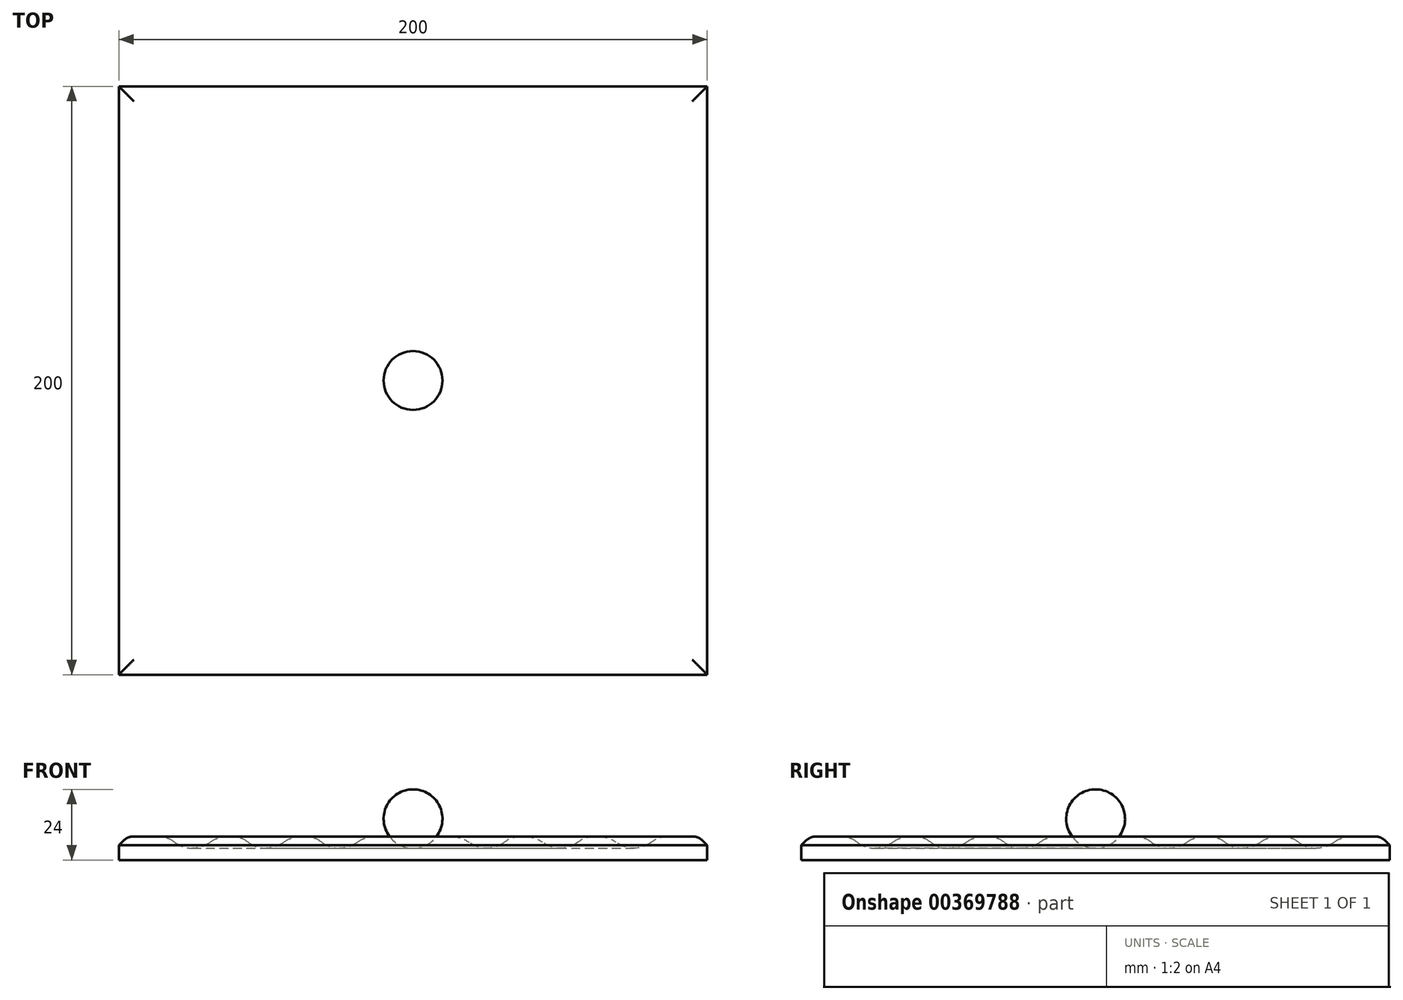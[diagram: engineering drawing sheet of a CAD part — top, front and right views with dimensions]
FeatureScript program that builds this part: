
annotation { "Feature Type Name" : "Feature", "Feature Type Description" : "" }
export const myFeature = defineFeature(function(context is Context, id is Id, definition is map)
    precondition{}
    {
        {
            var Q0;
            Q0=qCreatedBy(makeId("Top.planeOp"),FACE);
            var sketch = newSketch(context, id + "F0", { "sketchPlane" : qUnion([Q0])});
            skLineSegment(sketch, "E0.bottom", {"start": v(100, -100) * mm, "end": v(-100, -100) * mm});
            skLineSegment(sketch, "E0.top", {"start": v(100, 100) * mm, "end": v(-100, 100) * mm});
            skLineSegment(sketch, "E0.left", {"start": v(100, -100) * mm, "end": v(100, 100) * mm});
            skLineSegment(sketch, "E0.right", {"start": v(-100, -100) * mm, "end": v(-100, 100) * mm});
            skPoint(sketch, "E0.middle", {"position": v(0, 0) * mm});
            skCircle(sketch, "E1", {"center": v(0, 0) * mm, "radius": 90 * mm});
            skSolve(sketch);
        }
        {
            var Q0;
            Q0=makeQuery(id+"F0.imprint","IMPRINT",FACE,{"disambiguationData":[TD([[makeQuery(id+"F0.imprint","IMPRINT",EDGE,{"derivedFrom":sQuery(id+"F0.wireOp",EDGE,"E0.bottom")}),-1.0]])]});
            var Q1;
            Q1=makeQuery(id+"F0.imprint","IMPRINT",FACE,{"disambiguationData":[TD([[makeQuery(id+"F0.imprint","IMPRINT",EDGE,{"derivedFrom":sQuery(id+"F0.wireOp",EDGE,"E1")}),1.0]])]});
            extrude(context, id + "F1", {"entities" : qUnion([Q0, Q1]), "depth" : 8 * mm});
        }
        {
            var Q0;
            Q0=qCreatedBy(makeId("Front.planeOp"),FACE);
            var sketch = newSketch(context, id + "F2", { "sketchPlane" : qUnion([Q0])});
            skLineSegment(sketch, "E2", {"start": v(0, 0) * mm, "end": v(0, 24) * mm});
            skArc(sketch, "E3", {"start": v(0, 4) * mm, "mid": v(10, 14) * mm, "end": v(0, 24) * mm});
            skArc(sketch, "E4.1.0.0", {"start": v(25, 4) * mm, "mid": v(35, 14) * mm, "end": v(25, 24) * mm});
            skLineSegment(sketch, "E4.1.0.1", {"start": v(25, 0) * mm, "end": v(25, 24) * mm});
            skArc(sketch, "E4.2.0.0", {"start": v(50, 4) * mm, "mid": v(60, 14) * mm, "end": v(50, 24) * mm});
            skLineSegment(sketch, "E4.2.0.1", {"start": v(50, 0) * mm, "end": v(50, 24) * mm});
            skArc(sketch, "E4.3.0.0", {"start": v(75, 4) * mm, "mid": v(85, 14) * mm, "end": v(75, 24) * mm});
            skLineSegment(sketch, "E4.3.0.1", {"start": v(75, 0) * mm, "end": v(75, 24) * mm});
            skLineSegment(sketch, "E4.direction1", {"start": v(0, 4) * mm, "end": v(25, 4) * mm, "construction": true});
            skArc(sketch, "E5.1.0.0", {"start": v(-25, 4) * mm, "mid": v(-15, 14) * mm, "end": v(-25, 24) * mm});
            skLineSegment(sketch, "E5.1.0.1", {"start": v(-25, 0) * mm, "end": v(-25, 24) * mm});
            skArc(sketch, "E5.2.0.0", {"start": v(-50, 4) * mm, "mid": v(-40, 14) * mm, "end": v(-50, 24) * mm});
            skLineSegment(sketch, "E5.2.0.1", {"start": v(-50, 0) * mm, "end": v(-50, 24) * mm});
            skArc(sketch, "E5.3.0.0", {"start": v(-75, 4) * mm, "mid": v(-65, 14) * mm, "end": v(-75, 24) * mm});
            skLineSegment(sketch, "E5.3.0.1", {"start": v(-75, 0) * mm, "end": v(-75, 24) * mm});
            skLineSegment(sketch, "E5.direction1", {"start": v(0, 4) * mm, "end": v(-25, 4) * mm, "construction": true});
            skSolve(sketch);
        }
        {
            var Q0;
            {var subQ0=sQuery(id+"F2.wireOp",EDGE,"E3");Q0=makeQuery(id+"F2.imprint","IMPRINT",FACE,{"disambiguationData":[TD([[makeQuery(id+"F2.imprint","IMPRINT",EDGE,{"derivedFrom":subQ0}),1.0]])]});}
            var Q1;
            {var subQ0=sQuery(id+"F2.wireOp",EDGE,"E5.1.0.0");Q1=makeQuery(id+"F2.imprint","IMPRINT",FACE,{"disambiguationData":[TD([[makeQuery(id+"F2.imprint","IMPRINT",EDGE,{"derivedFrom":subQ0}),1.0]])]});}
            var Q2;
            {var subQ0=sQuery(id+"F2.wireOp",EDGE,"E5.2.0.0");Q2=makeQuery(id+"F2.imprint","IMPRINT",FACE,{"disambiguationData":[TD([[makeQuery(id+"F2.imprint","IMPRINT",EDGE,{"derivedFrom":subQ0}),1.0]])]});}
            var Q3;
            {var subQ0=sQuery(id+"F2.wireOp",EDGE,"E5.3.0.0");Q3=makeQuery(id+"F2.imprint","IMPRINT",FACE,{"disambiguationData":[TD([[makeQuery(id+"F2.imprint","IMPRINT",EDGE,{"derivedFrom":subQ0}),1.0]])]});}
            var Q4;
            {var subQ0=sQuery(id+"F2.wireOp",EDGE,"E4.1.0.0");Q4=makeQuery(id+"F2.imprint","IMPRINT",FACE,{"disambiguationData":[TD([[makeQuery(id+"F2.imprint","IMPRINT",EDGE,{"derivedFrom":subQ0}),1.0]])]});}
            var Q5;
            {var subQ0=sQuery(id+"F2.wireOp",EDGE,"E4.2.0.0");Q5=makeQuery(id+"F2.imprint","IMPRINT",FACE,{"disambiguationData":[TD([[makeQuery(id+"F2.imprint","IMPRINT",EDGE,{"derivedFrom":subQ0}),1.0]])]});}
            var Q6;
            {var subQ0=sQuery(id+"F2.wireOp",EDGE,"E4.3.0.0");Q6=makeQuery(id+"F2.imprint","IMPRINT",FACE,{"disambiguationData":[TD([[makeQuery(id+"F2.imprint","IMPRINT",EDGE,{"derivedFrom":subQ0}),1.0]])]});}
            var Q7;
            Q7=sQuery(id+"F2.wireOp",EDGE,"E2");
            revolve(context, id + "F3", {"entities" : qUnion([Q0, Q1, Q2, Q3, Q4, Q5, Q6]), "axis" : qUnion([Q7]), "revolveType" : RevolveType.FULL});
        }
        {
            var Q0;
            Q0=makeQuery(id+"F3.opRevolve","SWEPT_BODY",BODY,{"disambiguationData":[OSD([sQuery(id+"F2.wireOp",EDGE,"E4.1.0.0"),sQuery(id+"F2.wireOp",EDGE,"E4.1.0.1")])]});
            var Q1;
            Q1=makeQuery(id+"F3.opRevolve","SWEPT_BODY",BODY,{"disambiguationData":[OSD([sQuery(id+"F2.wireOp",EDGE,"E5.1.0.0"),sQuery(id+"F2.wireOp",EDGE,"E5.1.0.1")])]});
            var Q2;
            Q2=makeQuery(id+"F3.opRevolve","SWEPT_BODY",BODY,{"disambiguationData":[OSD([sQuery(id+"F2.wireOp",EDGE,"E5.2.0.0"),sQuery(id+"F2.wireOp",EDGE,"E5.2.0.1")])]});
            var Q3;
            Q3=makeQuery(id+"F3.opRevolve","SWEPT_BODY",BODY,{"disambiguationData":[OSD([sQuery(id+"F2.wireOp",EDGE,"E4.2.0.0"),sQuery(id+"F2.wireOp",EDGE,"E4.2.0.1")])]});
            var Q4;
            Q4=makeQuery(id+"F3.opRevolve","SWEPT_BODY",BODY,{"disambiguationData":[OSD([sQuery(id+"F2.wireOp",EDGE,"E5.3.0.0"),sQuery(id+"F2.wireOp",EDGE,"E5.3.0.1")])]});
            var Q5;
            Q5=makeQuery(id+"F3.opRevolve","SWEPT_BODY",BODY,{"disambiguationData":[OSD([sQuery(id+"F2.wireOp",EDGE,"E4.3.0.0"),sQuery(id+"F2.wireOp",EDGE,"E4.3.0.1")])]});
            var Q6;
            Q6=makeQuery(id+"F1.opExtrude","SWEPT_BODY",BODY,{"disambiguationData":[OSD([sQuery(id+"F0.wireOp",EDGE,"E0.bottom"),sQuery(id+"F0.wireOp",EDGE,"E0.top"),sQuery(id+"F0.wireOp",EDGE,"E0.left"),sQuery(id+"F0.wireOp",EDGE,"E0.right")])]});
            booleanBodies(context, id + "F4", {"operationType" : BooleanOperationType.SUBTRACTION, "tools" : qUnion([Q0, Q1, Q2, Q3, Q4, Q5]), "targets" : qUnion([Q6])});
        }
        {
            var Q0;
            Q0=makeQuery(id+"F4.opBoolean","INTERSECT",EDGE,{"disambiguationData":[OD(0.0)],"derivedFrom":[makeQuery(id+"F1.opExtrude","CAP_FACE",FACE,{"disambiguationData":[OSD([sQuery(id+"F0.wireOp",EDGE,"E0.bottom"),sQuery(id+"F0.wireOp",EDGE,"E0.top"),sQuery(id+"F0.wireOp",EDGE,"E0.left"),sQuery(id+"F0.wireOp",EDGE,"E0.right")])],"isStart":false}),makeQuery(id+"F3.opRevolve","SWEPT_FACE",FACE,{"disambiguationData":[OSD([sQuery(id+"F2.wireOp",EDGE,"E4.3.0.0")])]})]});
            var Q1;
            Q1=makeQuery(id+"F4.opBoolean","INTERSECT",EDGE,{"disambiguationData":[OD(1.0)],"derivedFrom":[makeQuery(id+"F1.opExtrude","CAP_FACE",FACE,{"disambiguationData":[OSD([sQuery(id+"F0.wireOp",EDGE,"E0.bottom"),sQuery(id+"F0.wireOp",EDGE,"E0.top"),sQuery(id+"F0.wireOp",EDGE,"E0.left"),sQuery(id+"F0.wireOp",EDGE,"E0.right")])],"isStart":false}),makeQuery(id+"F3.opRevolve","SWEPT_FACE",FACE,{"disambiguationData":[OSD([sQuery(id+"F2.wireOp",EDGE,"E4.3.0.0")])]})]});
            var Q2;
            Q2=makeQuery(id+"F4.opBoolean","INTERSECT",EDGE,{"disambiguationData":[OD(1.0)],"derivedFrom":[makeQuery(id+"F1.opExtrude","CAP_FACE",FACE,{"disambiguationData":[OSD([sQuery(id+"F0.wireOp",EDGE,"E0.bottom"),sQuery(id+"F0.wireOp",EDGE,"E0.top"),sQuery(id+"F0.wireOp",EDGE,"E0.left"),sQuery(id+"F0.wireOp",EDGE,"E0.right")])],"isStart":false}),makeQuery(id+"F3.opRevolve","SWEPT_FACE",FACE,{"disambiguationData":[OSD([sQuery(id+"F2.wireOp",EDGE,"E4.2.0.0")])]})]});
            var Q3;
            Q3=makeQuery(id+"F4.opBoolean","INTERSECT",EDGE,{"disambiguationData":[OD(0.0)],"derivedFrom":[makeQuery(id+"F1.opExtrude","CAP_FACE",FACE,{"disambiguationData":[OSD([sQuery(id+"F0.wireOp",EDGE,"E0.bottom"),sQuery(id+"F0.wireOp",EDGE,"E0.top"),sQuery(id+"F0.wireOp",EDGE,"E0.left"),sQuery(id+"F0.wireOp",EDGE,"E0.right")])],"isStart":false}),makeQuery(id+"F3.opRevolve","SWEPT_FACE",FACE,{"disambiguationData":[OSD([sQuery(id+"F2.wireOp",EDGE,"E4.2.0.0")])]})]});
            var Q4;
            Q4=makeQuery(id+"F4.opBoolean","INTERSECT",EDGE,{"disambiguationData":[OD(1.0)],"derivedFrom":[makeQuery(id+"F1.opExtrude","CAP_FACE",FACE,{"disambiguationData":[OSD([sQuery(id+"F0.wireOp",EDGE,"E0.bottom"),sQuery(id+"F0.wireOp",EDGE,"E0.top"),sQuery(id+"F0.wireOp",EDGE,"E0.left"),sQuery(id+"F0.wireOp",EDGE,"E0.right")])],"isStart":false}),makeQuery(id+"F3.opRevolve","SWEPT_FACE",FACE,{"disambiguationData":[OSD([sQuery(id+"F2.wireOp",EDGE,"E5.1.0.0")])]})]});
            var Q5;
            Q5=makeQuery(id+"F4.opBoolean","INTERSECT",EDGE,{"disambiguationData":[OD(0.0)],"derivedFrom":[makeQuery(id+"F1.opExtrude","CAP_FACE",FACE,{"disambiguationData":[OSD([sQuery(id+"F0.wireOp",EDGE,"E0.bottom"),sQuery(id+"F0.wireOp",EDGE,"E0.top"),sQuery(id+"F0.wireOp",EDGE,"E0.left"),sQuery(id+"F0.wireOp",EDGE,"E0.right")])],"isStart":false}),makeQuery(id+"F3.opRevolve","SWEPT_FACE",FACE,{"disambiguationData":[OSD([sQuery(id+"F2.wireOp",EDGE,"E5.1.0.0")])]})]});
            fillet(context, id + "F5", {"entities" : qUnion([Q0, Q1, Q2, Q3, Q4, Q5]), "radius" : 10 * mm, "tangentPropagation" : true, "allowEdgeOverflow" : false});
        }
        {
            var Q0;
            {var subQ0=sQuery(id+"F0.wireOp",EDGE,"E0.left");var subQ1=sQuery(id+"F0.wireOp",EDGE,"E0.top");var subQ2=sQuery(id+"F0.wireOp",EDGE,"E0.right");var subQ3=sQuery(id+"F0.wireOp",EDGE,"E0.bottom");Q0=makeQuery(id+"F4.opBoolean","SPLIT",FACE,{"disambiguationData":[TD([makeQuery(id+"F1.opExtrude","SWEPT_FACE",FACE,{"disambiguationData":[OSD([subQ3])]}),makeQuery(id+"F1.opExtrude","SWEPT_FACE",FACE,{"disambiguationData":[OSD([subQ1])]}),makeQuery(id+"F1.opExtrude","SWEPT_FACE",FACE,{"disambiguationData":[OSD([subQ0])]}),makeQuery(id+"F1.opExtrude","SWEPT_FACE",FACE,{"disambiguationData":[OSD([subQ2])]}),makeQuery(id+"F3.opRevolve","SWEPT_FACE",FACE,{"disambiguationData":[OSD([sQuery(id+"F2.wireOp",EDGE,"E4.3.0.0")])]}),makeQuery(id+"F3.opRevolve","SWEPT_FACE",FACE,{"disambiguationData":[OSD([sQuery(id+"F2.wireOp",EDGE,"E5.3.0.0")])]})])],"derivedFrom":makeQuery(id+"F1.opExtrude","CAP_FACE",FACE,{"disambiguationData":[OSD([subQ3,subQ1,subQ0,subQ2])],"isStart":false})});}
            chamfer(context, id + "F6", {"entities" : qUnion([Q0]), "width" : 3 * mm, "tangentPropagation" : true});
        }
        {
            var Q0;
            {var subQ0=sQuery(id+"F0.wireOp",EDGE,"E0.left");var subQ1=sQuery(id+"F0.wireOp",EDGE,"E0.top");var subQ2=sQuery(id+"F0.wireOp",EDGE,"E0.right");var subQ3=sQuery(id+"F0.wireOp",EDGE,"E0.bottom");Q0=makeQuery(id+"F4.opBoolean","SPLIT",FACE,{"disambiguationData":[TD([makeQuery(id+"F1.opExtrude","SWEPT_FACE",FACE,{"disambiguationData":[OSD([subQ3])]}),makeQuery(id+"F1.opExtrude","SWEPT_FACE",FACE,{"disambiguationData":[OSD([subQ1])]}),makeQuery(id+"F1.opExtrude","SWEPT_FACE",FACE,{"disambiguationData":[OSD([subQ0])]}),makeQuery(id+"F1.opExtrude","SWEPT_FACE",FACE,{"disambiguationData":[OSD([subQ2])]}),makeQuery(id+"F3.opRevolve","SWEPT_FACE",FACE,{"disambiguationData":[OSD([sQuery(id+"F2.wireOp",EDGE,"E4.3.0.0")])]}),makeQuery(id+"F3.opRevolve","SWEPT_FACE",FACE,{"disambiguationData":[OSD([sQuery(id+"F2.wireOp",EDGE,"E5.3.0.0")])]})])],"derivedFrom":makeQuery(id+"F1.opExtrude","CAP_FACE",FACE,{"disambiguationData":[OSD([subQ3,subQ1,subQ0,subQ2])],"isStart":false})});}
            fillet(context, id + "F7", {"entities" : qUnion([Q0]), "radius" : 5 * mm, "tangentPropagation" : true, "allowEdgeOverflow" : false});
        }
    });
